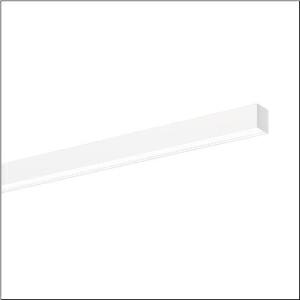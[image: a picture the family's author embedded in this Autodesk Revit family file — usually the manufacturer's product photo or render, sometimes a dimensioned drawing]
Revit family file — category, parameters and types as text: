
# Revit family: silica_r__21_51mx23dc4awb_8ea6
name_source: partatom
category: Lighting Fixtures
units: mm (PartAtom-declared; Revit-internal decimal feet)

## family parameters
Cut with Voids When Loaded = No
Host = Face
Light Source = No
Part Type = Normal
Room Calculation Point = No
Round Connector Dimension = Use Diameter
Shared = No

## types (1)
- --- (1 x LED, 8200 lm, 58.2 W, 4000K)
    Apparent Load = 58 VA
    CIE Flux Codes = 78 96 99 100 100
    Color Rendering = 80
    Color Temperature = 4000K
    Default Elevation = 1800 mm
    Description = Silica® 21, office luminaire, primary optical cover: prismatic diffuser, of PMMA, CAT 2 (L<= 3000cd/m²), light emission: direct distribution, primary light characteristic: symmetric, installation type: surface-mounted, LED, rated luminous flux: 8.200lm, luminous efficacy: 141lm/W, light colour: 840, colour temperature: 4000K, with terminal, 3+2-pole, max. 2.5mm², mains connection: 220..240V, AC, 50/60Hz, rated input power: 58.2W, luminaire housing, of aluminium, traffic white (RAL 9016), length: 3.004mm, width: 53mm, height: 53mm, protection rating (complete): IP20, insulation class (complete): insulation class I (protective earthing), certification: CE, permissible operating ambient temperature: 0..+35°C, standard: EN 50419, packaging unit: 1 piece
    Height = 0 mm  [stored 0 ft]
    Lamp = 1 x LED
    Lamp Light Flux = 8200 lm
    Lamp Power = 58.2 W
    Lamp count = 1
    Length = 3004 mm
    Luminous efficacy = 141 lm/W
    Manufacturer = Siteco
    ModVariant = No
    Model = 51MX23DC4AWB
    Mounting Place = Ceiling
    Mounting Type = Recessed
    Number of Poles = 1
    OnlyDefault = Yes
    Power Factor = 1
    Product Name = Silica® 21
    Product group = office luminaire | ceiling recessed
    ProductGroupID = 401
    Protection Class = Protection class I
    Protection Degree = IP 20
    RLX_Detail_Level = 1
    RLX_Emergency_Light_Flux = 0 lm
    RLX_Emergency_Type = 0
    RLX_Emergency_Type_DB = No
    RlxData = <blob elided: 18661 chars, md5=bd36af7b>
    Socket = socket
    Standby Power = 0 W
    System Light Flux = 8200 lm
    System Power = 58 W
    Type Comments = factory setting: luminous flux: 100 % | dim-lin: 254 | 323 mA
    Type Image = l_1313601.jpg
    URL = http://relux.com
    VarID = @adj_068275
    Voltage = 0 V
    Weight = 0.00 kg
    Width = 53 mm

note: [stored X ft] marks values corroborated as IEEE doubles in the binary element streams (Revit-internal decimal feet)

## geometry (parser evidence)
native form markers: Blend x4, Sweep x12
no freeform markers — native parametric forms only
